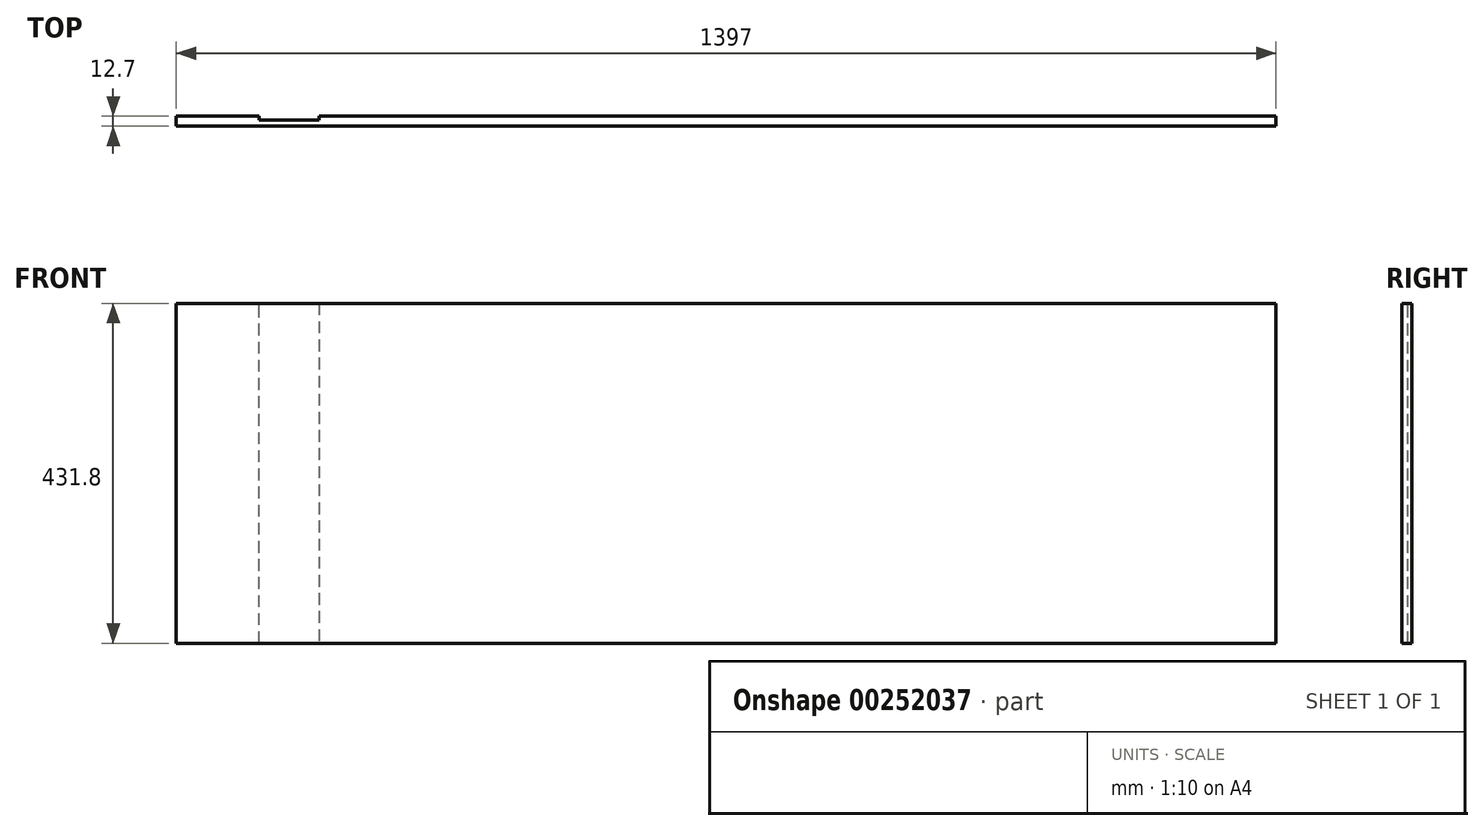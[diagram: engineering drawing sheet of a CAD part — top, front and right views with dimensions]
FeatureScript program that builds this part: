
annotation { "Feature Type Name" : "Feature", "Feature Type Description" : "" }
export const myFeature = defineFeature(function(context is Context, id is Id, definition is map)
    precondition{}
    {
        {
            var Q0;
            Q0=qCreatedBy(makeId("Front.planeOp"),FACE);
            var sketch = newSketch(context, id + "F0", { "sketchPlane" : qUnion([Q0])});
            skLineSegment(sketch, "E0", {"start": v(679.2, 121.57) * mm, "end": v(-717.8, 121.57) * mm});
            skLineSegment(sketch, "E1", {"start": v(-717.8, 121.57) * mm, "end": v(-717.8, -310.23) * mm});
            skLineSegment(sketch, "E2", {"start": v(-717.8, -310.23) * mm, "end": v(679.2, -310.23) * mm});
            skLineSegment(sketch, "E3", {"start": v(679.2, -310.23) * mm, "end": v(679.2, 121.57) * mm});
            skSolve(sketch);
        }
        {
            var Q0;
            Q0=makeQuery(id+"F0.imprint","IMPRINT",FACE,{"disambiguationData":[TD([[makeQuery(id+"F0.imprint","IMPRINT",EDGE,{"derivedFrom":sQuery(id+"F0.wireOp",EDGE,"E0")}),1.0]])]});
            extrude(context, id + "F1", {"entities" : qUnion([Q0]), "depth" : 12.7 * mm});
        }
        {
            var Q0;
            Q0=makeQuery(id+"F1.opExtrude","CAP_FACE",FACE,{"disambiguationData":[OSD([sQuery(id+"F0.wireOp",EDGE,"E0"),sQuery(id+"F0.wireOp",EDGE,"E1"),sQuery(id+"F0.wireOp",EDGE,"E2"),sQuery(id+"F0.wireOp",EDGE,"E3")])],"isStart":true});
            var sketch = newSketch(context, id + "F2", { "sketchPlane" : qUnion([Q0])});
            skLineSegment(sketch, "E4", {"start": v(612.35, -310.23) * mm, "end": v(612.35, 121.57) * mm});
            skLineSegment(sketch, "E5", {"start": v(612.35, 121.57) * mm, "end": v(536.15, 121.57) * mm});
            skLineSegment(sketch, "E6", {"start": v(536.15, 121.57) * mm, "end": v(536.15, -310.23) * mm});
            skLineSegment(sketch, "E7", {"start": v(536.15, -310.23) * mm, "end": v(612.35, -310.23) * mm});
            skSolve(sketch);
        }
        {
            var Q0;
            Q0=makeQuery(id+"F2.imprint","IMPRINT",FACE,{"disambiguationData":[TD([[makeQuery(id+"F2.imprint","IMPRINT",EDGE,{"derivedFrom":sQuery(id+"F2.wireOp",EDGE,"E4")}),1.0]])]});
            extrude(context, id + "F3", {"entities" : qUnion([Q0]), "operationType" : NewBodyOperationType.REMOVE, "oppositeDirection" : true, "depth" : 5.08 * mm});
        }
    });
